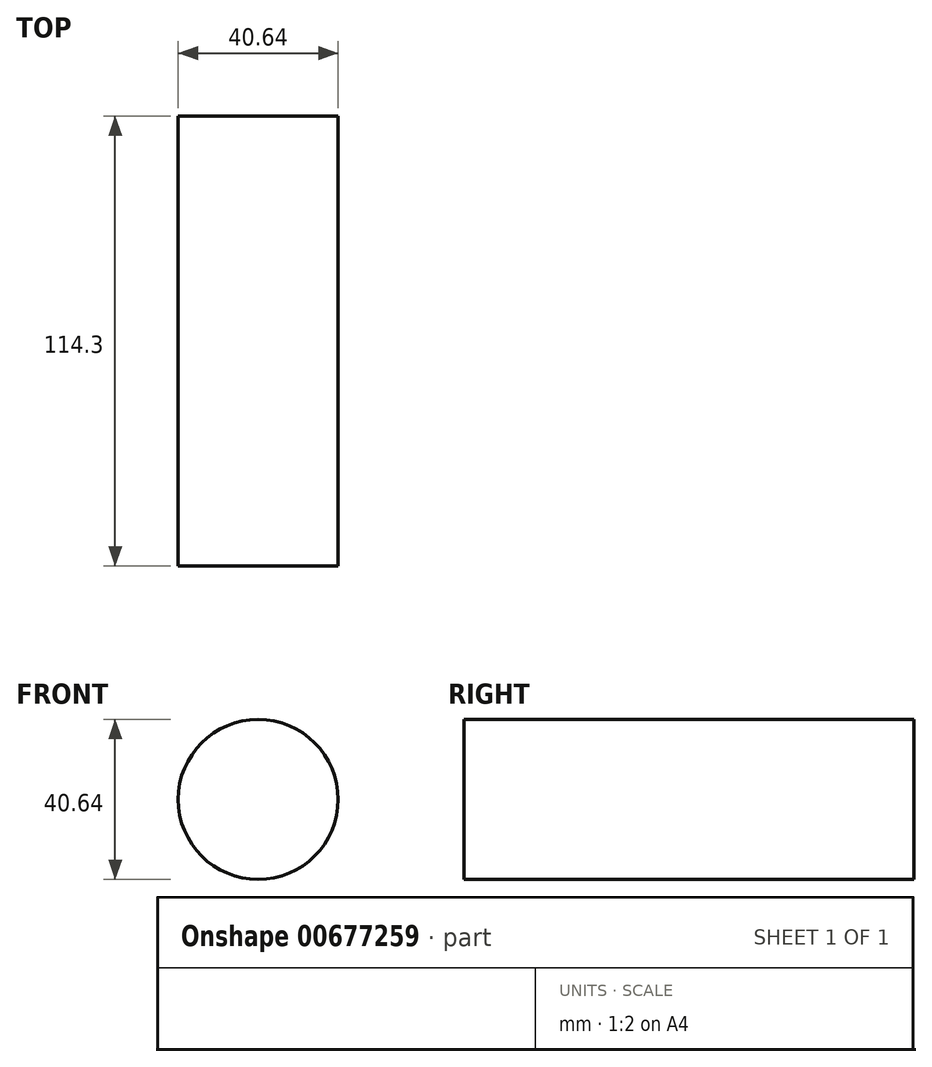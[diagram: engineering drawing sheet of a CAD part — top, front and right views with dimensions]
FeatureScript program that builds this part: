
annotation { "Feature Type Name" : "Feature", "Feature Type Description" : "" }
export const myFeature = defineFeature(function(context is Context, id is Id, definition is map)
    precondition{}
    {
        {
            var Q0;
            Q0=qCreatedBy(makeId("Front.planeOp"),FACE);
            var sketch = newSketch(context, id + "F0", { "sketchPlane" : qUnion([Q0])});
            skCircle(sketch, "E0", {"center": v(0, 0) * mm, "radius": 20.32 * mm});
            skSolve(sketch);
        }
        {
            var Q0;
            Q0=makeQuery(id+"F0.imprint","IMPRINT",FACE,{"disambiguationData":[TD([[makeQuery(id+"F0.imprint","IMPRINT",EDGE,{"derivedFrom":sQuery(id+"F0.wireOp",EDGE,"E0")}),1.0]])]});
            extrude(context, id + "F1", {"entities" : qUnion([Q0]), "endBound" : BoundingType.SYMMETRIC, "depth" : 114.3 * mm, "offsetDistance" : 25.4 * mm});
        }
    });
